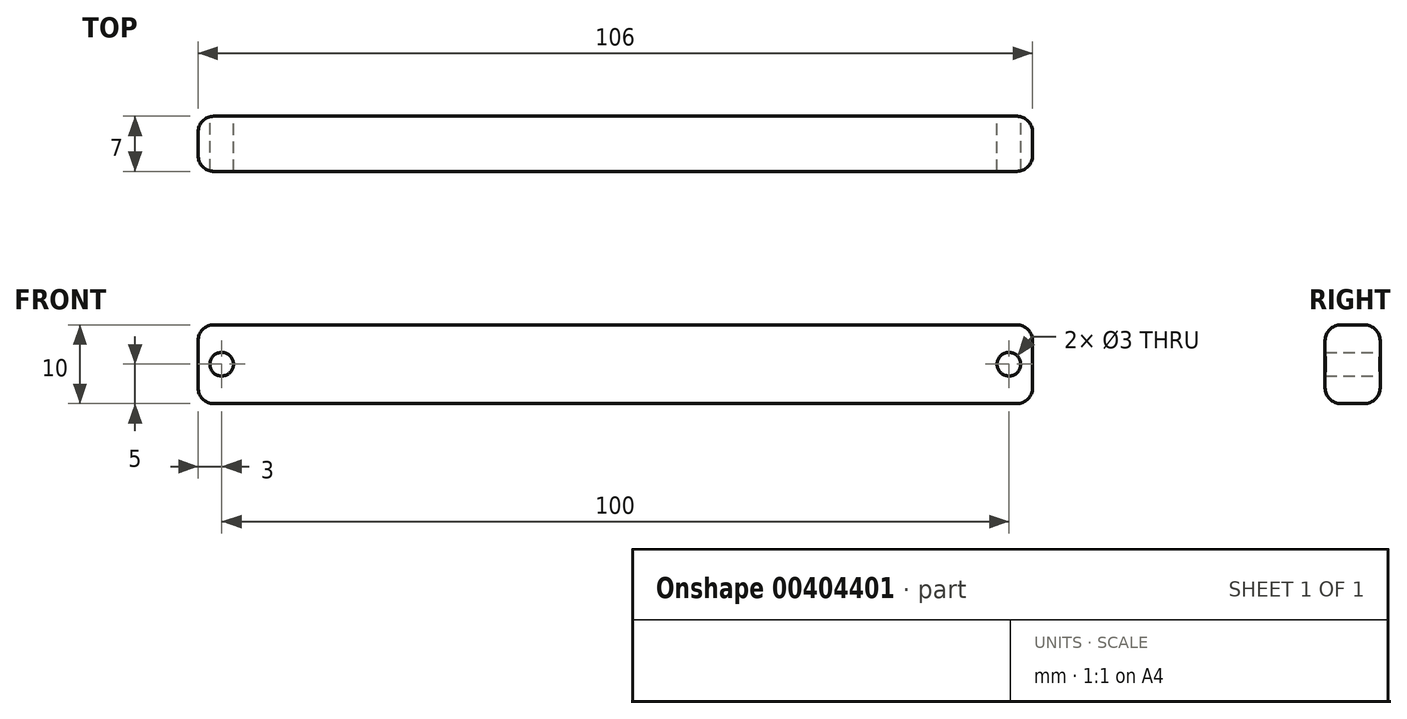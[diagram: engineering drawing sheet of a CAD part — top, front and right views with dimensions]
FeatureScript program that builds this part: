
annotation { "Feature Type Name" : "Feature", "Feature Type Description" : "" }
export const myFeature = defineFeature(function(context is Context, id is Id, definition is map)
    precondition{}
    {
        {
            var Q0;
            Q0=qCreatedBy(makeId("Front.planeOp"),FACE);
            var sketch = newSketch(context, id + "F0", { "sketchPlane" : qUnion([Q0])});
            skLineSegment(sketch, "E0.bottom", {"start": v(-53, 0) * mm, "end": v(53, 0) * mm});
            skLineSegment(sketch, "E0.top", {"start": v(-53, 10) * mm, "end": v(53, 10) * mm});
            skLineSegment(sketch, "E0.left", {"start": v(-53, 0) * mm, "end": v(-53, 10) * mm});
            skLineSegment(sketch, "E0.right", {"start": v(53, 0) * mm, "end": v(53, 10) * mm});
            skCircle(sketch, "E1", {"center": v(50, 5) * mm, "radius": 1.5 * mm});
            skCircle(sketch, "E2.1.0.0", {"center": v(-50, 5) * mm, "radius": 1.5 * mm});
            skLineSegment(sketch, "E2.direction1", {"start": v(50, 5) * mm, "end": v(-50, 5) * mm, "construction": true});
            skSolve(sketch);
        }
        {
            var Q0;
            Q0=makeQuery(id+"F0.imprint","IMPRINT",FACE,{"disambiguationData":[TD([[makeQuery(id+"F0.imprint","IMPRINT",EDGE,{"derivedFrom":sQuery(id+"F0.wireOp",EDGE,"E0.bottom")}),1.0]])]});
            var Q1;
            Q1=sQuery(id+"F0.wireOp",EDGE,"E0.top");
            extrude(context, id + "F1", {"entities" : qUnion([Q0]), "surfaceEntities" : qUnion([Q1]), "depth" : 7 * mm});
        }
        {
            var Q0;
            Q0=makeQuery(id+"F1.opExtrude","SWEPT_FACE",FACE,{"disambiguationData":[OSD([sQuery(id+"F0.wireOp",EDGE,"E0.right")])]});
            var Q1;
            Q1=makeQuery(id+"F1.opExtrude","SWEPT_FACE",FACE,{"disambiguationData":[OSD([sQuery(id+"F0.wireOp",EDGE,"E0.top")])]});
            fillet(context, id + "F2", {"entities" : qUnion([Q0, Q1]), "radius" : 2 * mm, "allowEdgeOverflow" : false});
        }
        {
            var Q0;
            Q0=makeQuery(id+"F1.opExtrude","SWEPT_FACE",FACE,{"disambiguationData":[OSD([sQuery(id+"F0.wireOp",EDGE,"E0.left")])]});
            var Q1;
            Q1=makeQuery(id+"F1.opExtrude","SWEPT_FACE",FACE,{"disambiguationData":[OSD([sQuery(id+"F0.wireOp",EDGE,"E0.bottom")])]});
            fillet(context, id + "F3", {"entities" : qUnion([Q0, Q1]), "radius" : 2 * mm, "tangentPropagation" : true, "allowEdgeOverflow" : false});
        }
    });
